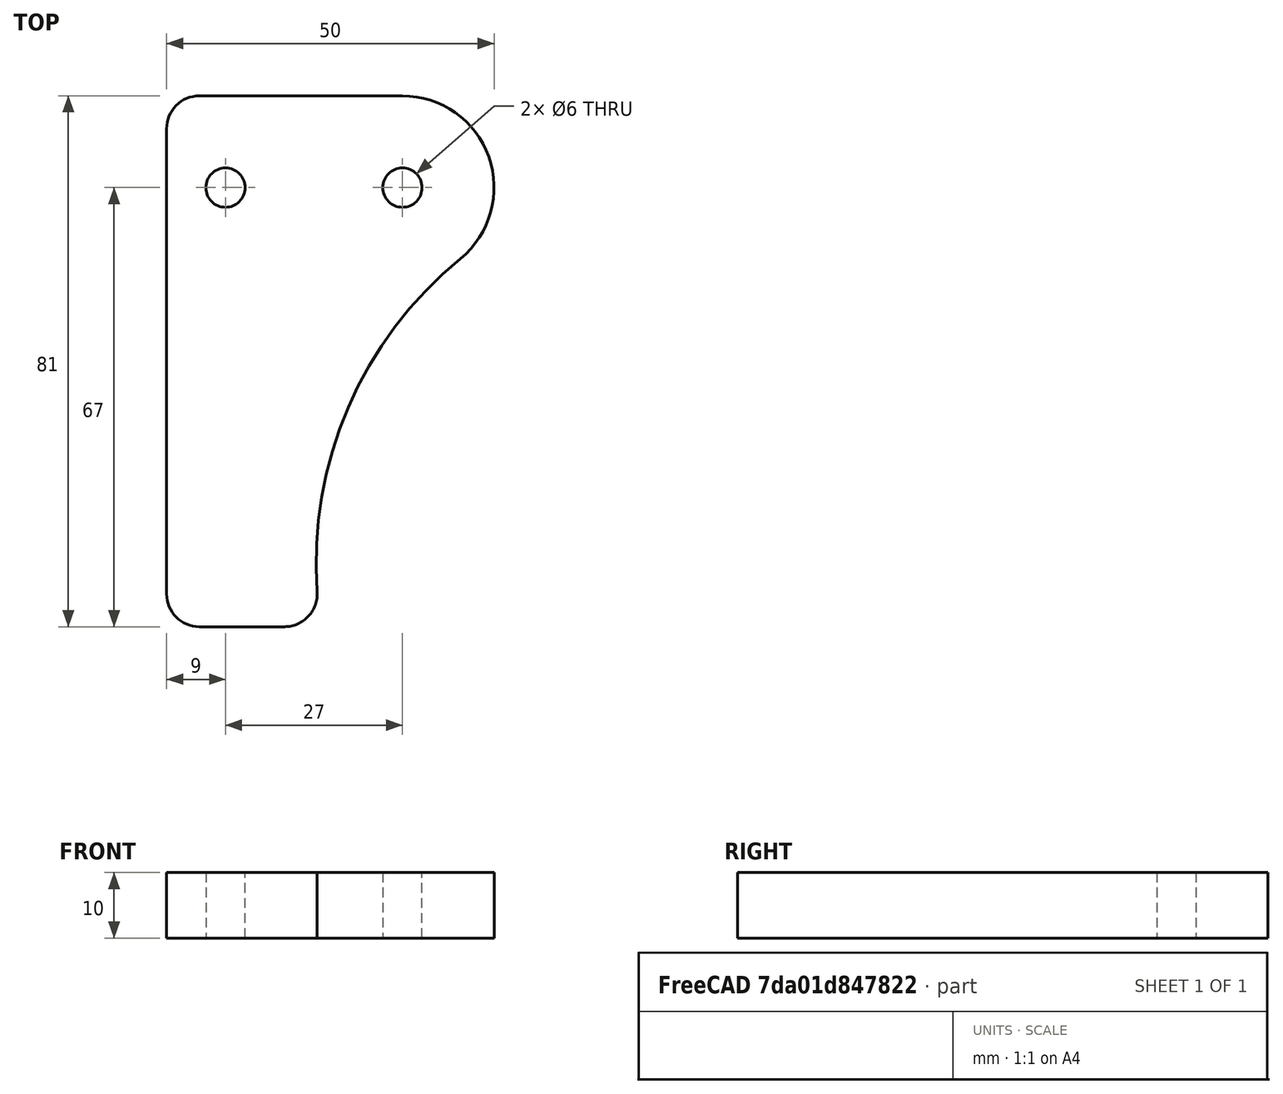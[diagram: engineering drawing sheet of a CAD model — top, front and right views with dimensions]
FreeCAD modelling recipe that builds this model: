
FCSTD DOCUMENT  (FreeCAD 0.19R23756 (Git))
Label: CLAMP_6
License: All rights reserved
LicenseURL: http://en.wikipedia.org/wiki/All_rights_reserved
objects: Sketcher::SketchObject×1, PartDesign::Pad×1, PartDesign::Body×1
note: 4 computed .brp shape members not serialized (recipe doc carries the construction recipe); baked Part::Feature solids carry a one-line shape summary decoded from their .brp

FEATURE [Sketcher::SketchObject] Sketch
  FullyConstrained = true
  MapMode = 5
  Support = -> [XY_Plane]
  sketch-geometry (10):
    g0: LineSegment StartX=-31 StartY=14 StartZ=0 EndX=3.6e-15 EndY=14 EndZ=0
    g1: ArcOfCircle CenterX=0 CenterY=0 CenterZ=0 NormalX=0 NormalY=0 NormalZ=1 AngleXU=0 Radius=14 StartAngle=5.39759 EndAngle=7.85398
    g2: ArcOfCircle CenterX=46.8297 CenterY=-57.2973 CenterZ=0 NormalX=0 NormalY=0 NormalZ=1 AngleXU=0 Radius=60 StartAngle=2.256 EndAngle=3.214
    g3: ArcOfCircle CenterX=-18 CenterY=-62 CenterZ=0 NormalX=0 NormalY=0 NormalZ=1 AngleXU=0 Radius=5 StartAngle=4.71239 EndAngle=6.3556
    g4: LineSegment StartX=-18 StartY=-67 StartZ=0 EndX=-31 EndY=-67 EndZ=0
    g5: ArcOfCircle CenterX=-31 CenterY=-62 CenterZ=0 NormalX=0 NormalY=0 NormalZ=1 AngleXU=0 Radius=5 StartAngle=3.14159 EndAngle=4.71239
    g6: LineSegment StartX=-36 StartY=-62 StartZ=0 EndX=-36 EndY=9 EndZ=0
    g7: ArcOfCircle CenterX=-31 CenterY=9 CenterZ=0 NormalX=0 NormalY=0 NormalZ=1 AngleXU=0 Radius=5 StartAngle=1.5708 EndAngle=3.14159
    g8: Circle CenterX=-27 CenterY=0 CenterZ=0 NormalX=0 NormalY=0 NormalZ=1 AngleXU=0 Radius=3
    g9: Circle CenterX=0 CenterY=0 CenterZ=0 NormalX=0 NormalY=0 NormalZ=1 AngleXU=0 Radius=3
  constraints (29):
    c: PointOnObject(g0,g-2)
    c: Tangent(g4,g5) = 1.5708
    c: Tangent(g5,g6) = 1.5708
    c: Vertical(g6)
    c: Horizontal(g4)
    c: Coincident(g-1,g1)
    c: Coincident(g0,g1)
    c: Horizontal(g0)
    c: Radius(g1) = 14
    c: Tangent(g6,g7) = 1.5708
    c: Tangent(g0,g7) = 1.5708
    c: Radius(g7) = 5
    c: Equal(g7,g5)
    c: Equal(g5,g3)
    c: Coincident(g2,g3)
    c: Coincident(g2,g1)
    c: Coincident(g3,g4)
    c: Tangent(g4,g3)
    c: DistanceY(g4,g-1) = 67
    c: Tangent(g3,g2)
    c: DistanceX(g5,g3) = 13
    c: Radius(g2) = 60
    c: Tangent(g2,g1)
    c: DistanceX(g6,g1) = 36
    c: PointOnObject(g8,g-1)
    c: Coincident(g9,g1)
    c: Equal(g8,g9)
    c: Diameter(g8) = 6
    c: DistanceX(g8,g1) = 27
FEATURE [PartDesign::Pad] Pad
  AllowMultiFace = false
  Direction = (1,1,1)
  Length = 10
  Length2 = 100
  Profile = -> Sketch
  Type = 0
FEATURE [PartDesign::Body] Body
  Group = -> [Sketch,Pad]
  Origin = -> Origin
  Tip = -> Pad
